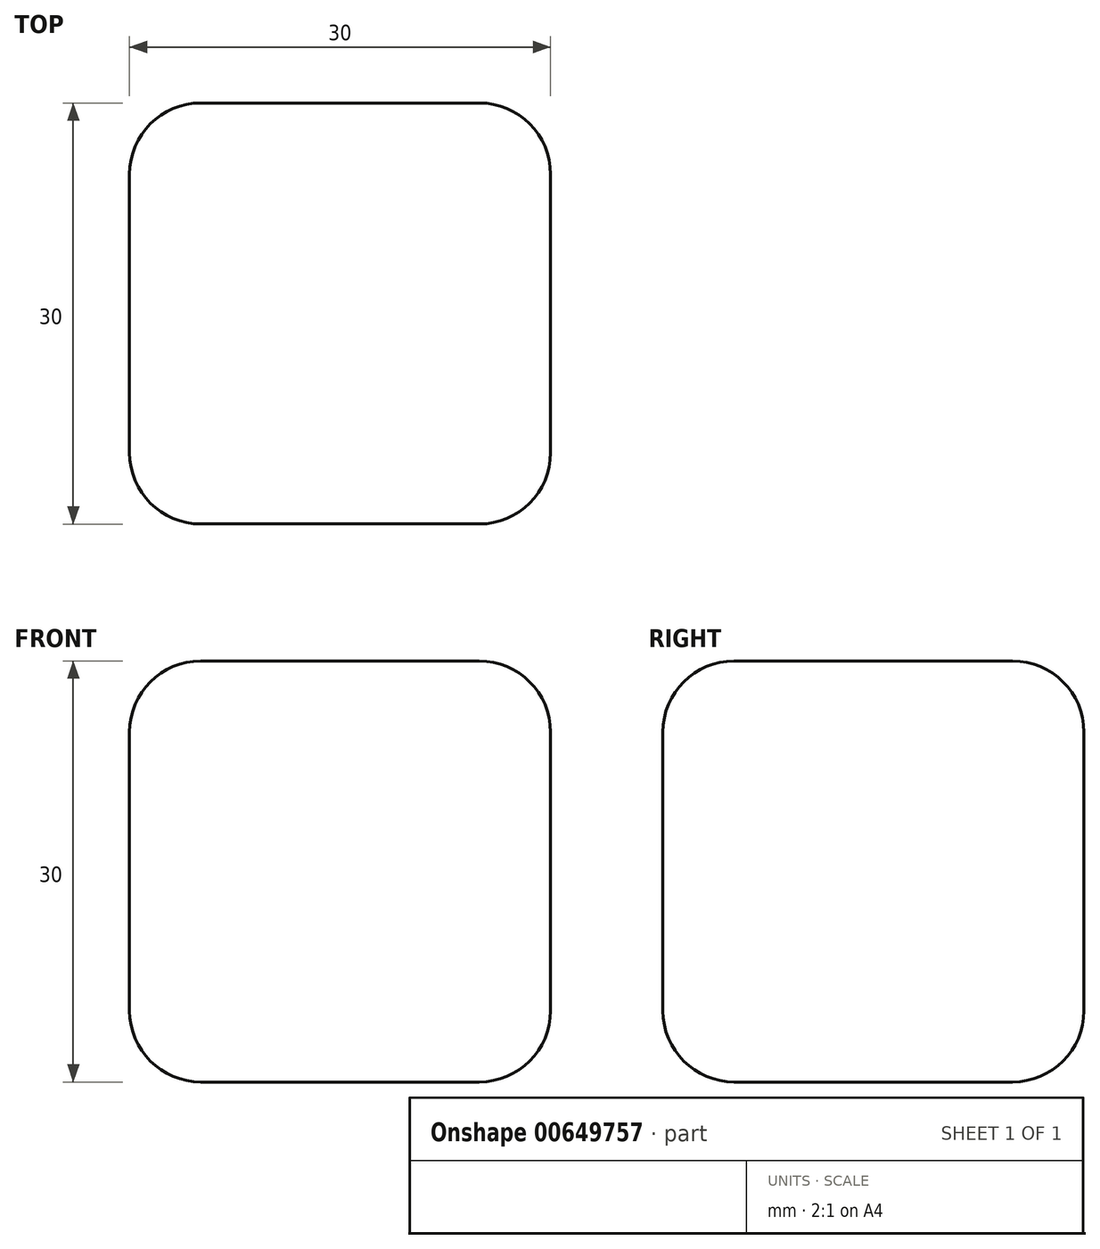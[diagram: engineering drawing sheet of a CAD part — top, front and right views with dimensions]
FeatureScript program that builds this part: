
annotation { "Feature Type Name" : "Feature", "Feature Type Description" : "" }
export const myFeature = defineFeature(function(context is Context, id is Id, definition is map)
    precondition{}
    {
        {
            var Q0;
            Q0=qCreatedBy(makeId("Top.planeOp"),FACE);
            var sketch = newSketch(context, id + "F0", { "sketchPlane" : qUnion([Q0])});
            skLineSegment(sketch, "E0.bottom", {"start": v(12.06, -6.33) * mm, "end": v(-17.94, -6.33) * mm});
            skLineSegment(sketch, "E0.top", {"start": v(12.06, 23.67) * mm, "end": v(-17.94, 23.67) * mm});
            skLineSegment(sketch, "E0.left", {"start": v(12.06, -6.33) * mm, "end": v(12.06, 23.67) * mm});
            skLineSegment(sketch, "E0.right", {"start": v(-17.94, -6.33) * mm, "end": v(-17.94, 23.67) * mm});
            skSolve(sketch);
        }
        {
            var Q0;
            Q0 = qSketchRegion(id + "F0", true);
            extrude(context, id + "F1", {"entities" : qUnion([Q0]), "depth" : 30 * mm, "offsetDistance" : 25.4 * mm});
        }
        {
            var Q0;
            Q0=makeQuery(id+"F1.opExtrude","SWEPT_EDGE",EDGE,{"disambiguationData":[OSD([sQuery(id+"F0.wireOp",EDGE,"E0.bottom"),sQuery(id+"F0.wireOp",EDGE,"E0.right")])]});
            var Q1;
            Q1=makeQuery(id+"F1.opExtrude","CAP_EDGE",EDGE,{"disambiguationData":[OSD([sQuery(id+"F0.wireOp",EDGE,"E0.top")])],"isStart":false});
            var Q2;
            Q2=makeQuery(id+"F1.opExtrude","CAP_EDGE",EDGE,{"disambiguationData":[OSD([sQuery(id+"F0.wireOp",EDGE,"E0.left")])],"isStart":false});
            var Q3;
            Q3=makeQuery(id+"F1.opExtrude","CAP_EDGE",EDGE,{"disambiguationData":[OSD([sQuery(id+"F0.wireOp",EDGE,"E0.bottom")])],"isStart":false});
            var Q4;
            Q4=makeQuery(id+"F1.opExtrude","CAP_EDGE",EDGE,{"disambiguationData":[OSD([sQuery(id+"F0.wireOp",EDGE,"E0.right")])],"isStart":false});
            var Q5;
            Q5=makeQuery(id+"F1.opExtrude","CAP_EDGE",EDGE,{"disambiguationData":[OSD([sQuery(id+"F0.wireOp",EDGE,"E0.right")])],"isStart":true});
            var Q6;
            Q6=makeQuery(id+"F1.opExtrude","SWEPT_EDGE",EDGE,{"disambiguationData":[OSD([sQuery(id+"F0.wireOp",EDGE,"E0.top"),sQuery(id+"F0.wireOp",EDGE,"E0.right")])]});
            var Q7;
            Q7=makeQuery(id+"F1.opExtrude","SWEPT_EDGE",EDGE,{"disambiguationData":[OSD([sQuery(id+"F0.wireOp",EDGE,"E0.top"),sQuery(id+"F0.wireOp",EDGE,"E0.left")])]});
            var Q8;
            Q8=makeQuery(id+"F1.opExtrude","CAP_EDGE",EDGE,{"disambiguationData":[OSD([sQuery(id+"F0.wireOp",EDGE,"E0.top")])],"isStart":true});
            var Q9;
            Q9=makeQuery(id+"F1.opExtrude","CAP_EDGE",EDGE,{"disambiguationData":[OSD([sQuery(id+"F0.wireOp",EDGE,"E0.left")])],"isStart":true});
            var Q10;
            Q10=makeQuery(id+"F1.opExtrude","CAP_EDGE",EDGE,{"disambiguationData":[OSD([sQuery(id+"F0.wireOp",EDGE,"E0.bottom")])],"isStart":true});
            var Q11;
            Q11=makeQuery(id+"F1.opExtrude","SWEPT_EDGE",EDGE,{"disambiguationData":[OSD([sQuery(id+"F0.wireOp",EDGE,"E0.bottom"),sQuery(id+"F0.wireOp",EDGE,"E0.left")])]});
            fillet(context, id + "F2", {"entities" : qUnion([Q0, Q1, Q2, Q3, Q4, Q5, Q6, Q7, Q8, Q9, Q10, Q11]), "radius" : 5.08 * mm, "tangentPropagation" : true, "allowEdgeOverflow" : false});
        }
    });
